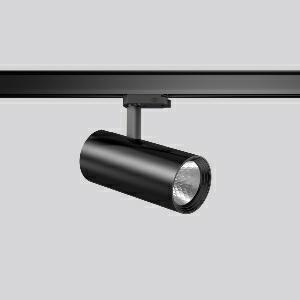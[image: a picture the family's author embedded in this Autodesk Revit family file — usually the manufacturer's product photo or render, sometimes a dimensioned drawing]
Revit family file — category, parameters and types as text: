
# Revit family: deecos_s_mini_742204_003_1_3ec5
name_source: partatom
category: Lighting Fixtures
units: mm (PartAtom-declared; Revit-internal decimal feet)

## family parameters
Cut with Voids When Loaded = No
Host = Face
Light Source = No
Part Type = Normal
Room Calculation Point = No
Round Connector Dimension = Use Diameter
Shared = No

## types (1)
- DEECOS S mini (1 x LED Modul 940, 3700 lm, 4000)
    Apparent Load = 29 VA
    Approval mark = CE
    CIE Flux Codes = 99 100 100 100 100
    Color Rendering = 92
    Color Temperature = 4000
    Default Elevation = 1800 mm
    Description = Series: DEECOS S mini
LED surface-mounted projector in modern design with no visible cooling ribs. Housing: die-cast aluminium, powder-coated. Rotation range: 356°. Swivel range: 90°. Black plastic ring and recessed LED to prevent glare from the side. Optical assembly with reflector made of MIRO-Silver with 98% total light reflection for outstanding efficiency - can be changed without tools. Best colour rendering index Ra>90. With multi adaptor for 3-circuit tracks 230 V. Suitable for Track on ceiling, Wall track. High quality converter without flickering and stroboscopic effect. The following accessories can be mounted without use of tools: interchangeable lenses, decorative glasses, honeycomb louvre, clear and frosted diffusers, white interchangeable plastic ring. 
Colour: deep black, matt (RAL 9005)
Diameter: 87 mm
Height: 214 mm
Lamp: LED
Socket: without socket
Colour temperature: 4000K
Colour rendering index (CRI): 92
System power: 29 W
Rated luminous flux: 3700 lm
Luminous efficiency: 128 lm/W
Control gear: Regulated power supply
Protection class: I
Type of protection: IP 20
    Height = 214 mm
    Lamp = 1 x LED Modul 940
    Lamp Light Flux = 3700 lm
    Lamp count = 1
    Length = 87 mm
    Lifetime = 50000 h
    Luminous efficacy = 128 lm/W
    Manufacturer = RZB
    ModVariant = No
    Model = 742204.003.1
    Mounting Place = Ceiling
    Mounting Type = Rail mounted
    Number of Poles = 1
    OnlyDefault = Yes
    Power Factor = 1
    Product Name = DEECOS S mini
    Product group = Track mounted projectors
    ProductGroupID = 301
    Protection Class = Protection class I
    Protection Degree = IP 20
    RLX_Detail_Level = 1
    RLX_Emergency_Light_Flux = 0 lm
    RLX_Emergency_Type = 0
    RLX_Emergency_Type_DB = No
    RlxData = <blob elided: 38909 chars, md5=27a1fc80>
    Socket = socket
    Standby Power = 0 W
    System Light Flux = 3700 lm
    System Power = 29 W
    Type Comments = Product without accessories
    Type Image = 741926.003.jpg
    URL = http://relux.com
    VarID = ---
    Voltage = 230 V
    Voltage Range = 220-240 V
    Weight = 0.00 kg
    Width = 0 mm  [stored 0 ft]

note: [stored X ft] marks values corroborated as IEEE doubles in the binary element streams (Revit-internal decimal feet)

## geometry (parser evidence)
native form markers: Blend x4, Sweep x13
no freeform markers — native parametric forms only
